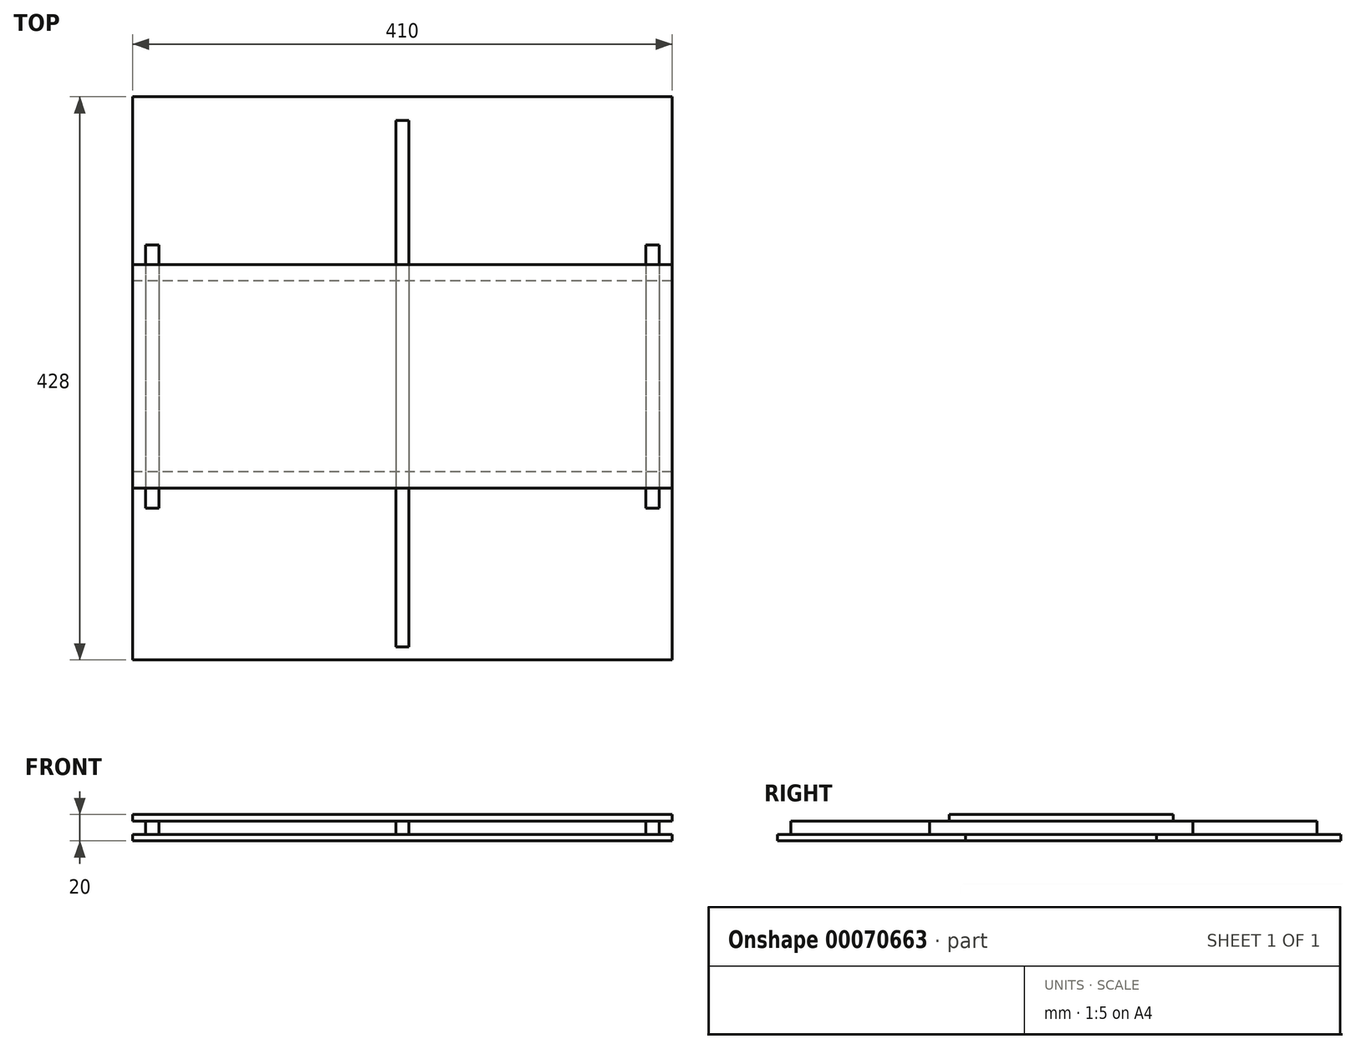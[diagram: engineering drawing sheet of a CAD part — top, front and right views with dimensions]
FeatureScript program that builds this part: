
annotation { "Feature Type Name" : "Feature", "Feature Type Description" : "" }
export const myFeature = defineFeature(function(context is Context, id is Id, definition is map)
    precondition{}
    {
        {
            var Q0;
            Q0=qCreatedBy(makeId("Top.planeOp"),FACE);
            var sketch = newSketch(context, id + "F0", { "sketchPlane" : qUnion([Q0])});
            skLineSegment(sketch, "E0.rect.bottom", {"start": v(205, 70) * mm, "end": v(-205, 70) * mm});
            skLineSegment(sketch, "E0.rect.top", {"start": v(205, -70) * mm, "end": v(-205, -70) * mm});
            skLineSegment(sketch, "E0.rect.left", {"start": v(205, 70) * mm, "end": v(205, -70) * mm});
            skLineSegment(sketch, "E0.rect.right", {"start": v(-205, 70) * mm, "end": v(-205, -70) * mm});
            skPoint(sketch, "E0.rect.middle", {"position": v(0, 0) * mm});
            skSolve(sketch);
        }
        {
            var Q0;
            Q0 = qSketchRegion(id + "F0", true);
            extrude(context, id + "F1", {"entities" : qUnion([Q0]), "depth" : 5 * mm});
        }
        {
            var Q0;
            Q0=makeQuery(id+"F1.opExtrude","SWEPT_FACE",FACE,{"disambiguationData":[OSD([sQuery(id+"F0.wireOp",EDGE,"E0.rect.top")])]});
            extrude(context, id + "F2", {"entities" : qUnion([Q0]), "depth" : 145 * mm});
        }
        {
            var Q0;
            Q0=makeQuery(id+"F2.opExtrude","CAP_FACE",FACE,{"disambiguationData":[OSD([sQuery(id+"F0.wireOp",EDGE,"E0.rect.top")])],"isStart":false});
            extrude(context, id + "F3", {"entities" : qUnion([Q0]), "depth" : 143 * mm});
        }
        {
            var Q0;
            Q0=makeQuery(id+"F1.opExtrude","CAP_FACE",FACE,{"disambiguationData":[OSD([sQuery(id+"F0.wireOp",EDGE,"E0.rect.bottom"),sQuery(id+"F0.wireOp",EDGE,"E0.rect.top"),sQuery(id+"F0.wireOp",EDGE,"E0.rect.left"),sQuery(id+"F0.wireOp",EDGE,"E0.rect.right")])],"isStart":false});
            var sketch = newSketch(context, id + "F4", { "sketchPlane" : qUnion([Q0])});
            skLineSegment(sketch, "E1.rect.bottom", {"start": v(5, 52) * mm, "end": v(-5, 52) * mm});
            skLineSegment(sketch, "E1.rect.top", {"start": v(5, -348) * mm, "end": v(-5, -348) * mm});
            skLineSegment(sketch, "E1.rect.left", {"start": v(5, 52) * mm, "end": v(5, -348) * mm});
            skLineSegment(sketch, "E1.rect.right", {"start": v(-5, 52) * mm, "end": v(-5, -348) * mm});
            skPoint(sketch, "E1.rect.middle", {"position": v(0, -148) * mm});
            skLineSegment(sketch, "E2.rect.bottom", {"start": v(195, -42.5) * mm, "end": v(185, -42.5) * mm});
            skLineSegment(sketch, "E2.rect.top", {"start": v(195, -242.5) * mm, "end": v(185, -242.5) * mm});
            skLineSegment(sketch, "E2.rect.left", {"start": v(195, -42.5) * mm, "end": v(195, -242.5) * mm});
            skLineSegment(sketch, "E2.rect.right", {"start": v(185, -42.5) * mm, "end": v(185, -242.5) * mm});
            skPoint(sketch, "E2.rect.middle", {"position": v(190, -142.5) * mm});
            skLineSegment(sketch, "E3.rect.bottom", {"start": v(-185, -42.5) * mm, "end": v(-195, -42.5) * mm});
            skLineSegment(sketch, "E3.rect.top", {"start": v(-185, -242.5) * mm, "end": v(-195, -242.5) * mm});
            skLineSegment(sketch, "E3.rect.left", {"start": v(-185, -42.5) * mm, "end": v(-185, -242.5) * mm});
            skLineSegment(sketch, "E3.rect.right", {"start": v(-195, -42.5) * mm, "end": v(-195, -242.5) * mm});
            skPoint(sketch, "E3.rect.middle", {"position": v(-190, -142.5) * mm});
            skLineSegment(sketch, "E4.0", {"start": v(-205, -215) * mm, "end": v(-205, -70) * mm, "construction": true});
            skPoint(sketch, "E5", {"position": v(-205, -142.5) * mm});
            skSolve(sketch);
        }
        {
            var Q0;
            Q0 = qSketchRegion(id + "F4", true);
            extrude(context, id + "F5", {"entities" : qUnion([Q0]), "depth" : 10 * mm});
        }
        {
            var Q0;
            Q0=makeQuery(id+"F5.opExtrude","CAP_FACE",FACE,{"disambiguationData":[OSD([sQuery(id+"F4.wireOp",EDGE,"E1.rect.bottom"),sQuery(id+"F4.wireOp",EDGE,"E1.rect.top"),sQuery(id+"F4.wireOp",EDGE,"E1.rect.left"),sQuery(id+"F4.wireOp",EDGE,"E1.rect.right")])],"isStart":false});
            var sketch = newSketch(context, id + "F6", { "sketchPlane" : qUnion([Q0])});
            skLineSegment(sketch, "E6.rect.bottom", {"start": v(205, -57.5) * mm, "end": v(-205, -57.5) * mm});
            skLineSegment(sketch, "E6.rect.top", {"start": v(205, -227.5) * mm, "end": v(-205, -227.5) * mm});
            skLineSegment(sketch, "E6.rect.left", {"start": v(205, -57.5) * mm, "end": v(205, -227.5) * mm});
            skLineSegment(sketch, "E6.rect.right", {"start": v(-205, -57.5) * mm, "end": v(-205, -227.5) * mm});
            skPoint(sketch, "E6.rect.middle", {"position": v(0, -142.5) * mm});
            skLineSegment(sketch, "E7.0", {"start": v(205, -215) * mm, "end": v(205, -70) * mm, "construction": true});
            skPoint(sketch, "E8", {"position": v(205, -142.5) * mm});
            skSolve(sketch);
        }
        {
            var Q0;
            Q0 = qSketchRegion(id + "F6", true);
            extrude(context, id + "F7", {"entities" : qUnion([Q0]), "depth" : 5 * mm});
        }
    });
